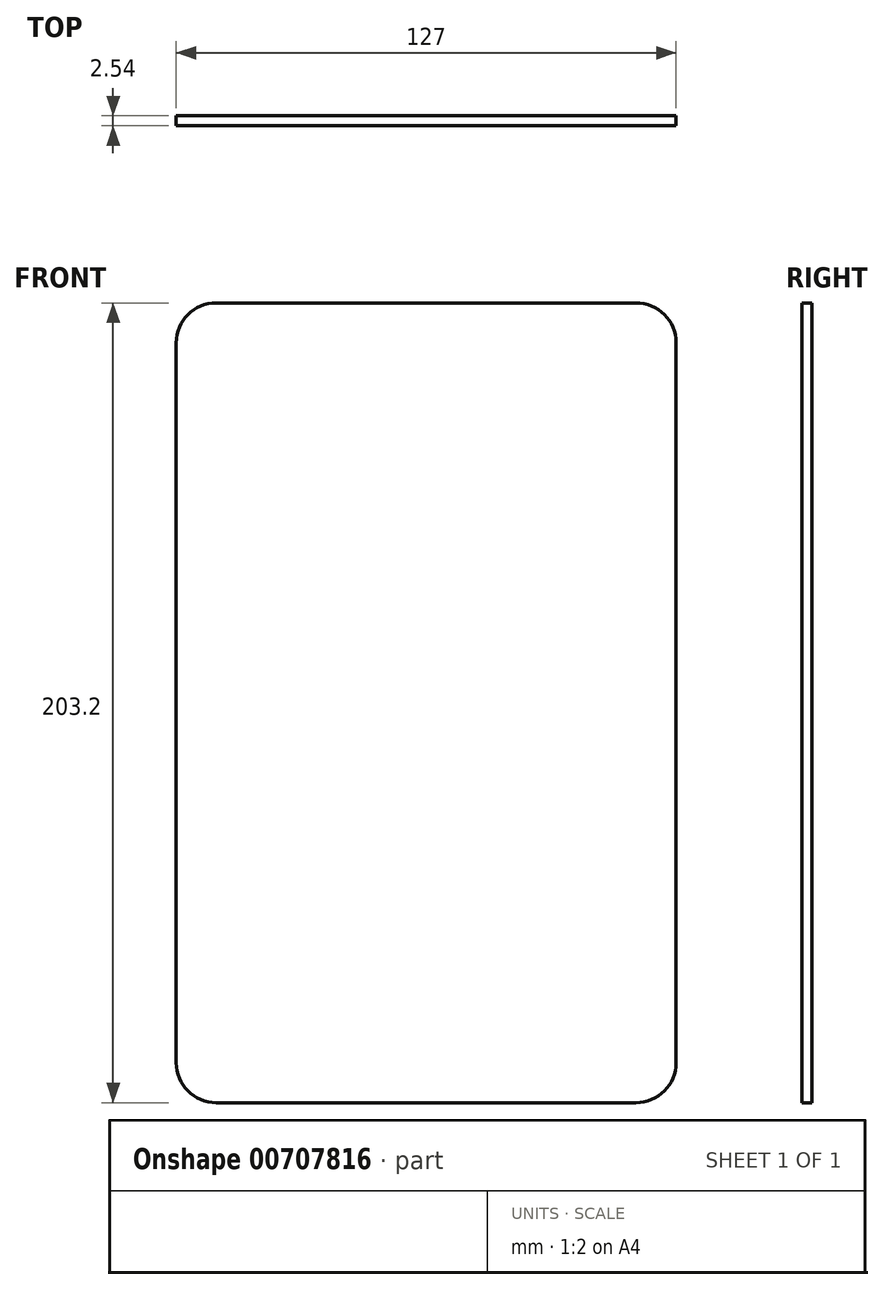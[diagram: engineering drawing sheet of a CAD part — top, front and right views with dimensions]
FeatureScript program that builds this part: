
annotation { "Feature Type Name" : "Feature", "Feature Type Description" : "" }
export const myFeature = defineFeature(function(context is Context, id is Id, definition is map)
    precondition{}
    {
        {
            var Q0;
            Q0=qCreatedBy(makeId("Front.planeOp"),FACE);
            var sketch = newSketch(context, id + "F0", { "sketchPlane" : qUnion([Q0])});
            skLineSegment(sketch, "E0.bottom", {"start": v(-63.5, -101.6) * mm, "end": v(63.5, -101.6) * mm});
            skLineSegment(sketch, "E0.top", {"start": v(-63.5, 101.6) * mm, "end": v(63.5, 101.6) * mm});
            skLineSegment(sketch, "E0.left", {"start": v(-63.5, -101.6) * mm, "end": v(-63.5, 101.6) * mm});
            skLineSegment(sketch, "E0.right", {"start": v(63.5, -101.6) * mm, "end": v(63.5, 101.6) * mm});
            skPoint(sketch, "E0.middle", {"position": v(0, 0) * mm});
            skSolve(sketch);
        }
        {
            var Q0;
            Q0 = qSketchRegion(id + "F0", true);
            extrude(context, id + "F1", {"entities" : qUnion([Q0]), "endBound" : BoundingType.SYMMETRIC, "depth" : 2.54 * mm, "offsetDistance" : 25.4 * mm});
        }
        {
            var Q0;
            Q0=makeQuery(id+"F1.opExtrude","SWEPT_EDGE",EDGE,{"disambiguationData":[OSD([sQuery(id+"F0.wireOp",EDGE,"E0.top"),sQuery(id+"F0.wireOp",EDGE,"E0.left")])]});
            var Q1;
            Q1=makeQuery(id+"F1.opExtrude","SWEPT_EDGE",EDGE,{"disambiguationData":[OSD([sQuery(id+"F0.wireOp",EDGE,"E0.top"),sQuery(id+"F0.wireOp",EDGE,"E0.right")])]});
            var Q2;
            Q2=makeQuery(id+"F1.opExtrude","SWEPT_EDGE",EDGE,{"disambiguationData":[OSD([sQuery(id+"F0.wireOp",EDGE,"E0.bottom"),sQuery(id+"F0.wireOp",EDGE,"E0.right")])]});
            var Q3;
            Q3=makeQuery(id+"F1.opExtrude","SWEPT_EDGE",EDGE,{"disambiguationData":[OSD([sQuery(id+"F0.wireOp",EDGE,"E0.bottom"),sQuery(id+"F0.wireOp",EDGE,"E0.left")])]});
            fillet(context, id + "F2", {"entities" : qUnion([Q0, Q1, Q2, Q3]), "radius" : 10.16 * mm, "tangentPropagation" : true, "allowEdgeOverflow" : false});
        }
    });
